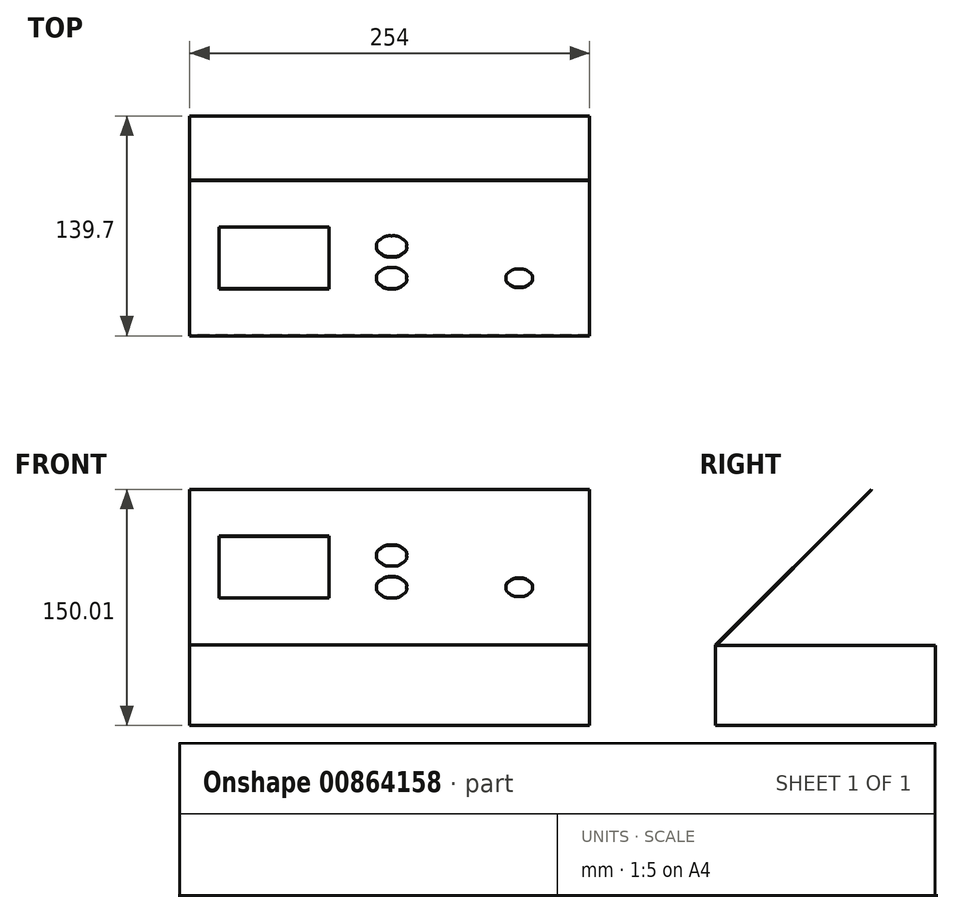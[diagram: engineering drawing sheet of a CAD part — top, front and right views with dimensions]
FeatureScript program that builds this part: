
annotation { "Feature Type Name" : "Feature", "Feature Type Description" : "" }
export const myFeature = defineFeature(function(context is Context, id is Id, definition is map)
    precondition{}
    {
        {
            var Q0;
            Q0=qCreatedBy(makeId("Right.planeOp"),FACE);
            var sketch = newSketch(context, id + "F0", { "sketchPlane" : qUnion([Q0])});
            skLineSegment(sketch, "E0.bottom", {"start": v(0, 0) * mm, "end": v(-139.7, 0) * mm});
            skLineSegment(sketch, "E0.top", {"start": v(0, 50.8) * mm, "end": v(-139.3, 50.8) * mm});
            skLineSegment(sketch, "E0.left", {"start": v(0, 0) * mm, "end": v(0, 50.8) * mm});
            skLineSegment(sketch, "E0.right", {"start": v(-139.7, 0) * mm, "end": v(-139.7, 51.22) * mm});
            skLineSegment(sketch, "E1", {"start": v(-139.7, 51.22) * mm, "end": v(-40.92, 150) * mm});
            skLineSegment(sketch, "E2", {"start": v(-40.92, 150) * mm, "end": v(-40.63, 149.72) * mm});
            skLineSegment(sketch, "E3", {"start": v(-40.63, 149.72) * mm, "end": v(-139.3, 51.05) * mm});
            skLineSegment(sketch, "E4", {"start": v(-139.3, 50.8) * mm, "end": v(-139.3, 51.05) * mm});
            skLineSegment(sketch, "E5", {"start": v(-139.3, 50.8) * mm, "end": v(-139.7, 50.8) * mm, "construction": true});
            skSolve(sketch);
        }
        {
            var Q0;
            Q0=qSketchRegion(id+"F0",true);
            extrude(context, id + "F1", {"entities" : qUnion([Q0]), "endBound" : BoundingType.SYMMETRIC, "depth" : 254 * mm, "offsetDistance" : 25.4 * mm});
        }
        {
            var Q0;
            Q0=makeQuery(id+"F1.opExtrude","SWEPT_FACE",FACE,{"disambiguationData":[OSD([sQuery(id+"F0.wireOp",EDGE,"E1")])]});
            var sketch = newSketch(context, id + "F2", { "sketchPlane" : qUnion([Q0])});
            skLineSegment(sketch, "E6", {"start": v(-127.35, -62.39) * mm, "end": v(-127.35, 76.52) * mm, "construction": true});
            skLineSegment(sketch, "E7", {"start": v(126.65, -62.39) * mm, "end": v(126.65, 76.52) * mm, "construction": true});
            skLineSegment(sketch, "E8", {"start": v(-127.35, 76.52) * mm, "end": v(126.65, 76.52) * mm, "construction": true});
            skLineSegment(sketch, "E9", {"start": v(-108.3, -20.32) * mm, "end": v(-38.45, -20.32) * mm});
            skLineSegment(sketch, "E10", {"start": v(-108.3, 35.24) * mm, "end": v(-108.3, -20.32) * mm});
            skLineSegment(sketch, "E11", {"start": v(-38.45, 35.24) * mm, "end": v(-108.3, 35.24) * mm});
            skLineSegment(sketch, "E12", {"start": v(-38.45, -20.32) * mm, "end": v(-38.45, 35.24) * mm});
            skLineSegment(sketch, "E13", {"start": v(-38.45, -14.45) * mm, "end": v(-38.45, 1.76) * mm});
            skLineSegment(sketch, "E14", {"start": v(-108.3, -14.45) * mm, "end": v(-108.3, 1.76) * mm});
            skLineSegment(sketch, "E15", {"start": v(126.65, -62.39) * mm, "end": v(-127.35, -62.39) * mm, "construction": true});
            skFitSpline(sketch, "E16", {"points": [v(1.23, -1.27) * mm, v(-1.26, -1.27) * mm, v(-3.74, -2.3) * mm, v(-5.5, -4.06) * mm]});
            skFitSpline(sketch, "E17", {"points": [v(-5.5, -4.06) * mm, v(-7.26, -5.82) * mm, v(-8.3, -8.3) * mm, v(-8.3, -10.8) * mm, v(-8.3, -13.29) * mm, v(-7.26, -15.77) * mm, v(-5.5, -17.53) * mm]});
            skFitSpline(sketch, "E18", {"points": [v(-5.5, -17.53) * mm, v(-3.74, -19.3) * mm, v(-1.26, -20.32) * mm, v(1.23, -20.32) * mm, v(3.73, -20.32) * mm, v(6.2, -19.3) * mm, v(7.97, -17.53) * mm]});
            skFitSpline(sketch, "E19", {"points": [v(7.97, -17.53) * mm, v(9.73, -15.77) * mm, v(10.76, -13.29) * mm, v(10.76, -10.8) * mm, v(10.76, -8.3) * mm, v(9.73, -5.82) * mm, v(7.97, -4.06) * mm]});
            skFitSpline(sketch, "E20", {"points": [v(7.97, -4.06) * mm, v(6.2, -2.3) * mm, v(3.73, -1.27) * mm, v(1.23, -1.27) * mm]});
            skFitSpline(sketch, "E21", {"points": [v(1.23, 27.3) * mm, v(-1.26, 27.3) * mm, v(-3.74, 26.28) * mm, v(-5.5, 24.51) * mm]});
            skFitSpline(sketch, "E22", {"points": [v(-5.5, 24.51) * mm, v(-7.26, 22.75) * mm, v(-8.3, 20.27) * mm, v(-8.3, 17.78) * mm, v(-8.3, 15.29) * mm, v(-7.26, 12.8) * mm, v(-5.5, 11.04) * mm]});
            skFitSpline(sketch, "E23", {"points": [v(-5.5, 11.04) * mm, v(-3.74, 9.28) * mm, v(-1.26, 8.26) * mm, v(1.23, 8.26) * mm, v(3.73, 8.26) * mm, v(6.2, 9.28) * mm, v(7.97, 11.04) * mm]});
            skFitSpline(sketch, "E24", {"points": [v(7.97, 11.04) * mm, v(9.73, 12.8) * mm, v(10.76, 15.29) * mm, v(10.76, 17.78) * mm, v(10.76, 20.27) * mm, v(9.73, 22.75) * mm, v(7.97, 24.51) * mm]});
            skFitSpline(sketch, "E25", {"points": [v(7.97, 24.51) * mm, v(6.2, 26.28) * mm, v(3.73, 27.3) * mm, v(1.23, 27.3) * mm]});
            skFitSpline(sketch, "E26", {"points": [v(82.2, -2.46) * mm, v(80.02, -2.46) * mm, v(77.85, -3.36) * mm, v(76.3, -4.9) * mm]});
            skFitSpline(sketch, "E27", {"points": [v(76.3, -4.9) * mm, v(74.76, -6.45) * mm, v(73.86, -8.61) * mm, v(73.86, -10.8) * mm, v(73.86, -12.98) * mm, v(74.76, -15.15) * mm, v(76.3, -16.69) * mm]});
            skFitSpline(sketch, "E28", {"points": [v(76.3, -16.69) * mm, v(77.85, -18.23) * mm, v(80.02, -19.13) * mm, v(82.2, -19.13) * mm, v(84.38, -19.13) * mm, v(86.55, -18.23) * mm, v(88.1, -16.69) * mm]});
            skFitSpline(sketch, "E29", {"points": [v(88.1, -16.69) * mm, v(89.63, -15.15) * mm, v(90.53, -12.98) * mm, v(90.53, -10.8) * mm, v(90.53, -8.61) * mm, v(89.63, -6.45) * mm, v(88.1, -4.9) * mm]});
            skFitSpline(sketch, "E30", {"points": [v(88.1, -4.9) * mm, v(86.55, -3.36) * mm, v(84.38, -2.46) * mm, v(82.2, -2.46) * mm]});
            skSolve(sketch);
        }
        {
            var Q0;
            Q0=qSketchRegion(id+"F2",true);
            var Q1;
            Q1=makeQuery(id+"F1.opExtrude","SWEPT_FACE",FACE,{"disambiguationData":[OSD([sQuery(id+"F0.wireOp",EDGE,"E3")])]});
            extrude(context, id + "F3", {"entities" : qUnion([Q0]), "operationType" : NewBodyOperationType.REMOVE, "endBound" : BoundingType.UP_TO_SURFACE, "oppositeDirection" : true, "depth" : 25.4 * mm, "endBoundEntityFace" : qUnion([Q1]), "offsetDistance" : 25.4 * mm});
        }
    });
